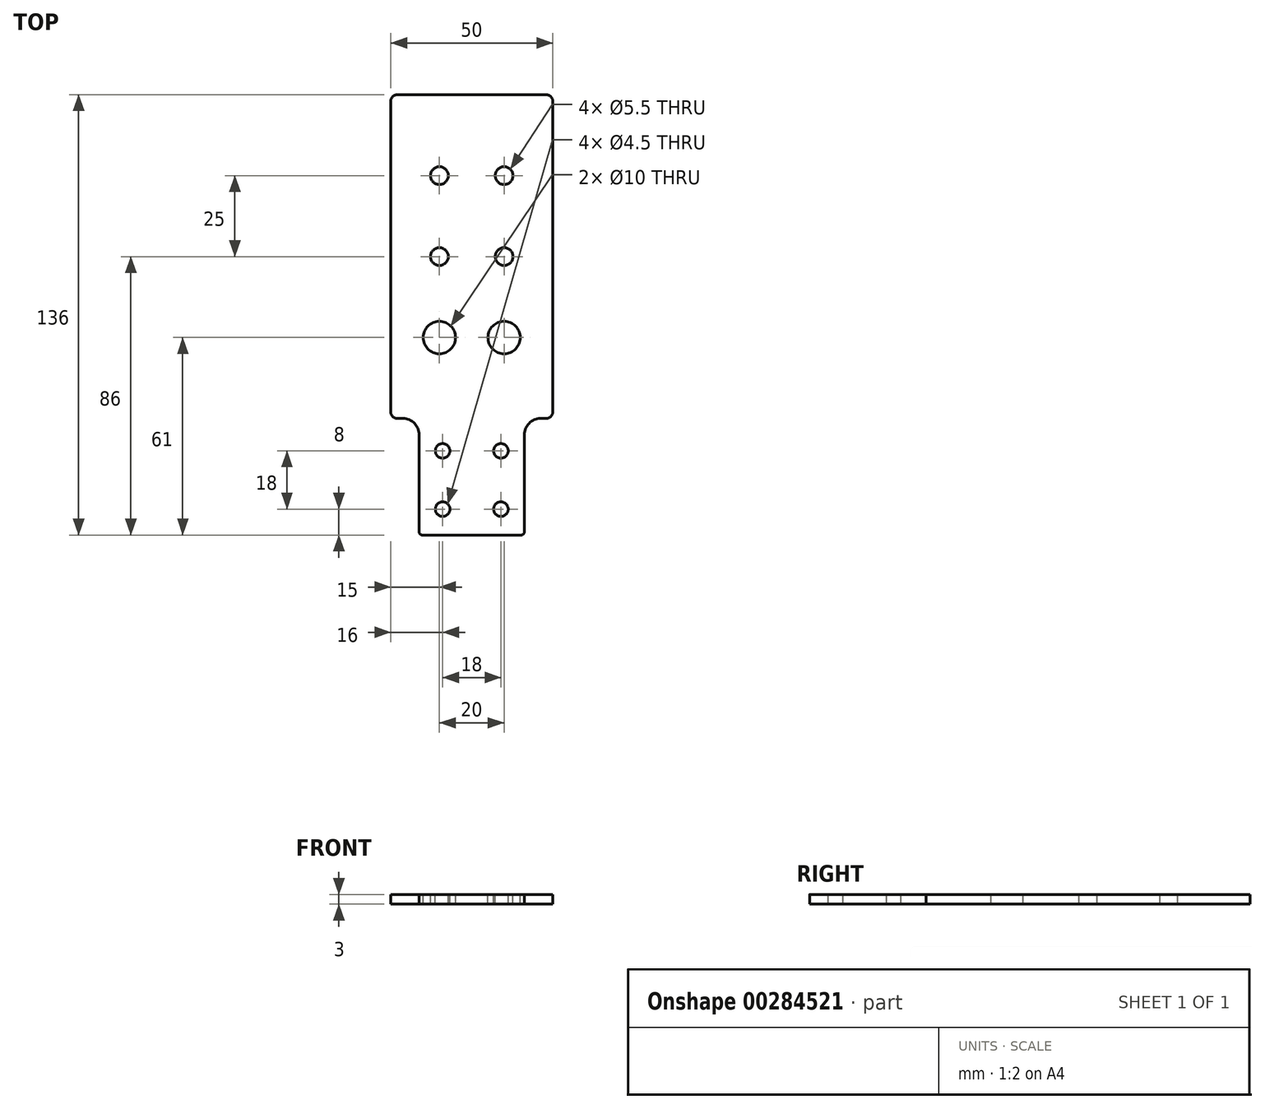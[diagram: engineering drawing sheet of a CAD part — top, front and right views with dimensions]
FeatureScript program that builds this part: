
annotation { "Feature Type Name" : "Feature", "Feature Type Description" : "" }
export const myFeature = defineFeature(function(context is Context, id is Id, definition is map)
    precondition{}
    {
        {
            var Q0;
            Q0=qCreatedBy(makeId("Top.planeOp"),FACE);
            var sketch = newSketch(context, id + "F0", { "sketchPlane" : qUnion([Q0])});
            skLineSegment(sketch, "E0.top", {"start": v(23, 50) * mm, "end": v(-23, 50) * mm});
            skLineSegment(sketch, "E0.left", {"start": v(25, -48) * mm, "end": v(25, 48) * mm});
            skLineSegment(sketch, "E0.right", {"start": v(-25, -48) * mm, "end": v(-25, 48) * mm});
            skPoint(sketch, "E0.middle", {"position": v(0, 0) * mm});
            skLineSegment(sketch, "E1", {"start": v(16.25, -55) * mm, "end": v(16.25, -86) * mm});
            skLineSegment(sketch, "E2", {"start": v(16.25, -86) * mm, "end": v(0, -86) * mm});
            skLineSegment(sketch, "E3", {"start": v(0, -86) * mm, "end": v(-16.25, -86) * mm});
            skLineSegment(sketch, "E4", {"start": v(-16.25, -86) * mm, "end": v(-16.25, -55) * mm});
            skLineSegment(sketch, "E5", {"start": v(21.25, -50) * mm, "end": v(23, -50) * mm});
            skLineSegment(sketch, "E6", {"start": v(-21.25, -50) * mm, "end": v(-23, -50) * mm});
            skPoint(sketch, "E7.visualSharp", {"position": v(-16.25, -50) * mm});
            skArc(sketch, "E7.filletArc", {"start": v(-16.25, -55) * mm, "mid": v(-17.71, -51.46) * mm, "end": v(-21.25, -50) * mm});
            skPoint(sketch, "E8.visualSharp", {"position": v(16.25, -50) * mm});
            skArc(sketch, "E8.filletArc", {"start": v(21.25, -50) * mm, "mid": v(17.71, -51.46) * mm, "end": v(16.25, -55) * mm});
            skPoint(sketch, "E9.visualSharp", {"position": v(-25, -50) * mm});
            skArc(sketch, "E9.filletArc", {"start": v(-25, -48) * mm, "mid": v(-24.41, -49.41) * mm, "end": v(-23, -50) * mm});
            skPoint(sketch, "E10.visualSharp", {"position": v(25, -50) * mm});
            skArc(sketch, "E10.filletArc", {"start": v(23, -50) * mm, "mid": v(24.41, -49.41) * mm, "end": v(25, -48) * mm});
            skPoint(sketch, "E11.visualSharp", {"position": v(-25, 50) * mm});
            skArc(sketch, "E11.filletArc", {"start": v(-23, 50) * mm, "mid": v(-24.41, 49.41) * mm, "end": v(-25, 48) * mm});
            skPoint(sketch, "E12.visualSharp", {"position": v(25, 50) * mm});
            skArc(sketch, "E12.filletArc", {"start": v(25, 48) * mm, "mid": v(24.41, 49.41) * mm, "end": v(23, 50) * mm});
            skSolve(sketch);
        }
        {
            var Q0;
            Q0=makeQuery(id+"F0.imprint","IMPRINT",FACE,{"disambiguationData":[TD([[makeQuery(id+"F0.imprint","IMPRINT",EDGE,{"derivedFrom":sQuery(id+"F0.wireOp",EDGE,"E0.top")}),1.0]])]});
            extrude(context, id + "F1", {"entities" : qUnion([Q0]), "depth" : 3 * mm});
        }
        {
            var Q0;
            Q0=makeQuery(id+"F1.opExtrude","CAP_FACE",FACE,{"disambiguationData":[OSD([sQuery(id+"F0.wireOp",EDGE,"E0.bottom"),sQuery(id+"F0.wireOp",EDGE,"E0.top"),sQuery(id+"F0.wireOp",EDGE,"E0.left"),sQuery(id+"F0.wireOp",EDGE,"E0.right")])],"isStart":false});
            var sketch = newSketch(context, id + "F2", { "sketchPlane" : qUnion([Q0])});
            skCircle(sketch, "E13", {"center": v(-10, -25) * mm, "radius": 5 * mm});
            skCircle(sketch, "E14", {"center": v(-10, 0) * mm, "radius": 2.75 * mm});
            skCircle(sketch, "E15", {"center": v(-10, 25) * mm, "radius": 2.75 * mm});
            skCircle(sketch, "E16", {"center": v(10, 25) * mm, "radius": 2.75 * mm});
            skCircle(sketch, "E17", {"center": v(10, 0) * mm, "radius": 2.75 * mm});
            skCircle(sketch, "E18", {"center": v(10, -25) * mm, "radius": 5 * mm});
            skLineSegment(sketch, "E19", {"start": v(-10, -25) * mm, "end": v(10, -25) * mm, "construction": true});
            skLineSegment(sketch, "E20", {"start": v(10, 0) * mm, "end": v(10, -25) * mm, "construction": true});
            skLineSegment(sketch, "E21", {"start": v(10, 0) * mm, "end": v(-10, 0) * mm, "construction": true});
            skLineSegment(sketch, "E22", {"start": v(-10, -25) * mm, "end": v(-10, 0) * mm, "construction": true});
            skLineSegment(sketch, "E23", {"start": v(-10, 0) * mm, "end": v(-10, 25) * mm, "construction": true});
            skLineSegment(sketch, "E24", {"start": v(10, 25) * mm, "end": v(10, 0) * mm, "construction": true});
            skLineSegment(sketch, "E25", {"start": v(10, 25) * mm, "end": v(-10, 25) * mm, "construction": true});
            skPoint(sketch, "E26", {"position": v(0, 0) * mm});
            skSolve(sketch);
        }
        {
            var Q0;
            Q0 = qSketchRegion(id + "F2", true);
            extrude(context, id + "F3", {"entities" : qUnion([Q0]), "operationType" : NewBodyOperationType.REMOVE, "endBound" : BoundingType.UP_TO_NEXT, "oppositeDirection" : true, "depth" : 25 * mm});
        }
        {
            var Q0;
            Q0=makeQuery(id+"F1.opExtrude","CAP_FACE",FACE,{"disambiguationData":[OSD([sQuery(id+"F0.wireOp",EDGE,"E0.top"),sQuery(id+"F0.wireOp",EDGE,"E0.left"),sQuery(id+"F0.wireOp",EDGE,"E0.right"),sQuery(id+"F0.wireOp",EDGE,"E1"),sQuery(id+"F0.wireOp",EDGE,"E2"),sQuery(id+"F0.wireOp",EDGE,"E3"),sQuery(id+"F0.wireOp",EDGE,"E4"),sQuery(id+"F0.wireOp",EDGE,"E5"),sQuery(id+"F0.wireOp",EDGE,"E6"),sQuery(id+"F0.wireOp",EDGE,"E7.filletArc"),sQuery(id+"F0.wireOp",EDGE,"E8.filletArc"),sQuery(id+"F0.wireOp",EDGE,"E9.filletArc"),sQuery(id+"F0.wireOp",EDGE,"E10.filletArc"),sQuery(id+"F0.wireOp",EDGE,"E11.filletArc"),sQuery(id+"F0.wireOp",EDGE,"E12.filletArc")])],"isStart":false});
            var sketch = newSketch(context, id + "F4", { "sketchPlane" : qUnion([Q0])});
            skLineSegment(sketch, "E27.bottom", {"start": v(9, -78) * mm, "end": v(-9, -78) * mm, "construction": true});
            skLineSegment(sketch, "E27.top", {"start": v(9, -60) * mm, "end": v(-9, -60) * mm, "construction": true});
            skLineSegment(sketch, "E27.left", {"start": v(9, -78) * mm, "end": v(9, -60) * mm, "construction": true});
            skLineSegment(sketch, "E27.right", {"start": v(-9, -78) * mm, "end": v(-9, -60) * mm, "construction": true});
            skPoint(sketch, "E27.middle", {"position": v(0, -69) * mm});
            skCircle(sketch, "E28", {"center": v(-9, -60) * mm, "radius": 2.25 * mm});
            skCircle(sketch, "E29", {"center": v(9, -60) * mm, "radius": 2.25 * mm});
            skCircle(sketch, "E30", {"center": v(9, -78) * mm, "radius": 2.25 * mm});
            skCircle(sketch, "E31", {"center": v(-9, -78) * mm, "radius": 2.25 * mm});
            skSolve(sketch);
        }
        {
            var Q0;
            Q0 = qSketchRegion(id + "F4", true);
            extrude(context, id + "F5", {"entities" : qUnion([Q0]), "operationType" : NewBodyOperationType.REMOVE, "endBound" : BoundingType.UP_TO_NEXT, "oppositeDirection" : true, "depth" : 25 * mm});
        }
        {
            var Q0;
            Q0=makeQuery(id+"F1.opExtrude","SWEPT_EDGE",EDGE,{"disambiguationData":[OSD([sQuery(id+"F0.wireOp",EDGE,"E3"),sQuery(id+"F0.wireOp",EDGE,"E4")])]});
            var Q1;
            Q1=makeQuery(id+"F1.opExtrude","SWEPT_EDGE",EDGE,{"disambiguationData":[OSD([sQuery(id+"F0.wireOp",EDGE,"E1"),sQuery(id+"F0.wireOp",EDGE,"E2")])]});
            fillet(context, id + "F6", {"entities" : qUnion([Q0, Q1]), "radius" : 1 * mm, "tangentPropagation" : true, "allowEdgeOverflow" : false});
        }
    });
